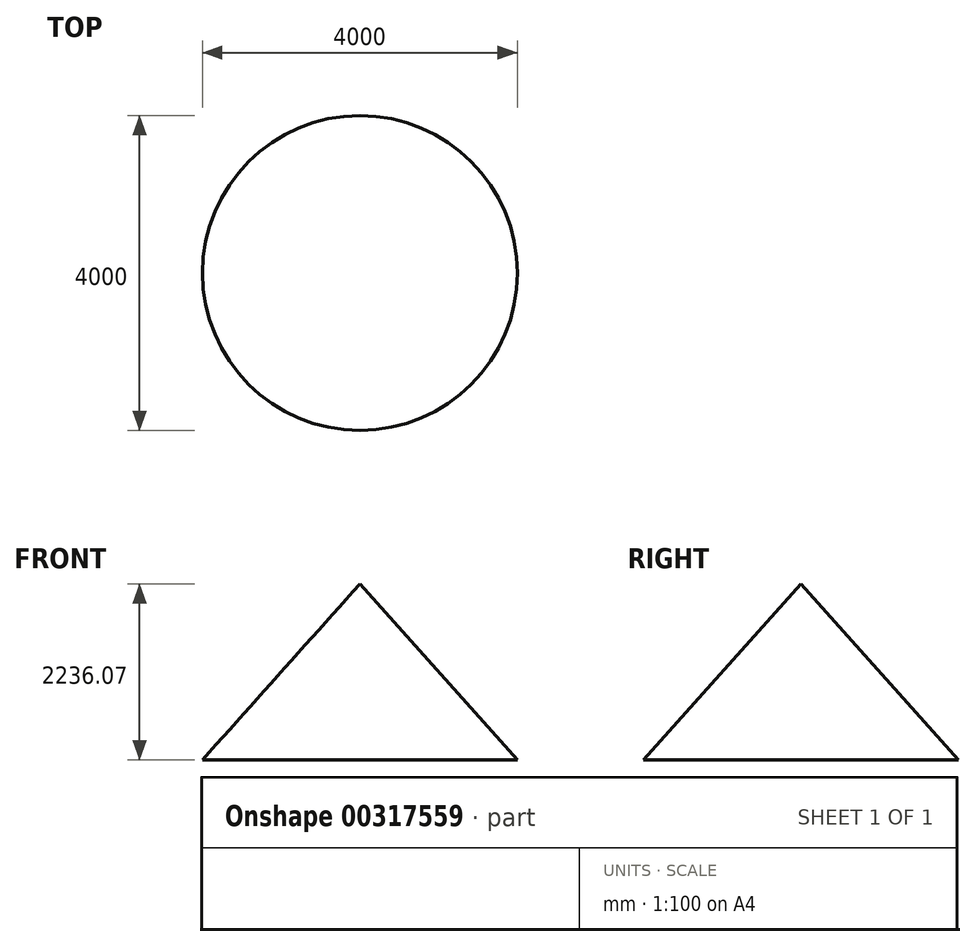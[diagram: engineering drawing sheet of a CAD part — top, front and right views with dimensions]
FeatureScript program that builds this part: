
annotation { "Feature Type Name" : "Feature", "Feature Type Description" : "" }
export const myFeature = defineFeature(function(context is Context, id is Id, definition is map)
    precondition{}
    {
        {
            var Q0;
            Q0=qCreatedBy(makeId("Front.planeOp"),FACE);
            var sketch = newSketch(context, id + "F0", { "sketchPlane" : qUnion([Q0])});
            skLineSegment(sketch, "E0", {"start": v(0, 0) * mm, "end": v(0, 2236.07) * mm});
            skLineSegment(sketch, "E1", {"start": v(0, 0) * mm, "end": v(2000, 0) * mm});
            skLineSegment(sketch, "E2", {"start": v(2000, 0) * mm, "end": v(0, 2236.07) * mm});
            skLineSegment(sketch, "E3", {"start": v(0, 0) * mm, "end": v(0, 2903.9) * mm, "construction": true});
            skSolve(sketch);
        }
        {
            var Q0;
            Q0=makeQuery(id+"F0.imprint","IMPRINT",FACE,{"disambiguationData":[TD([[makeQuery(id+"F0.imprint","IMPRINT",EDGE,{"derivedFrom":sQuery(id+"F0.wireOp",EDGE,"E0")}),-1.0]])]});
            var Q1;
            Q1=sQuery(id+"F0.wireOp",EDGE,"E3");
            revolve(context, id + "F1", {"entities" : qUnion([Q0]), "axis" : qUnion([Q1]), "revolveType" : RevolveType.FULL});
        }
    });
